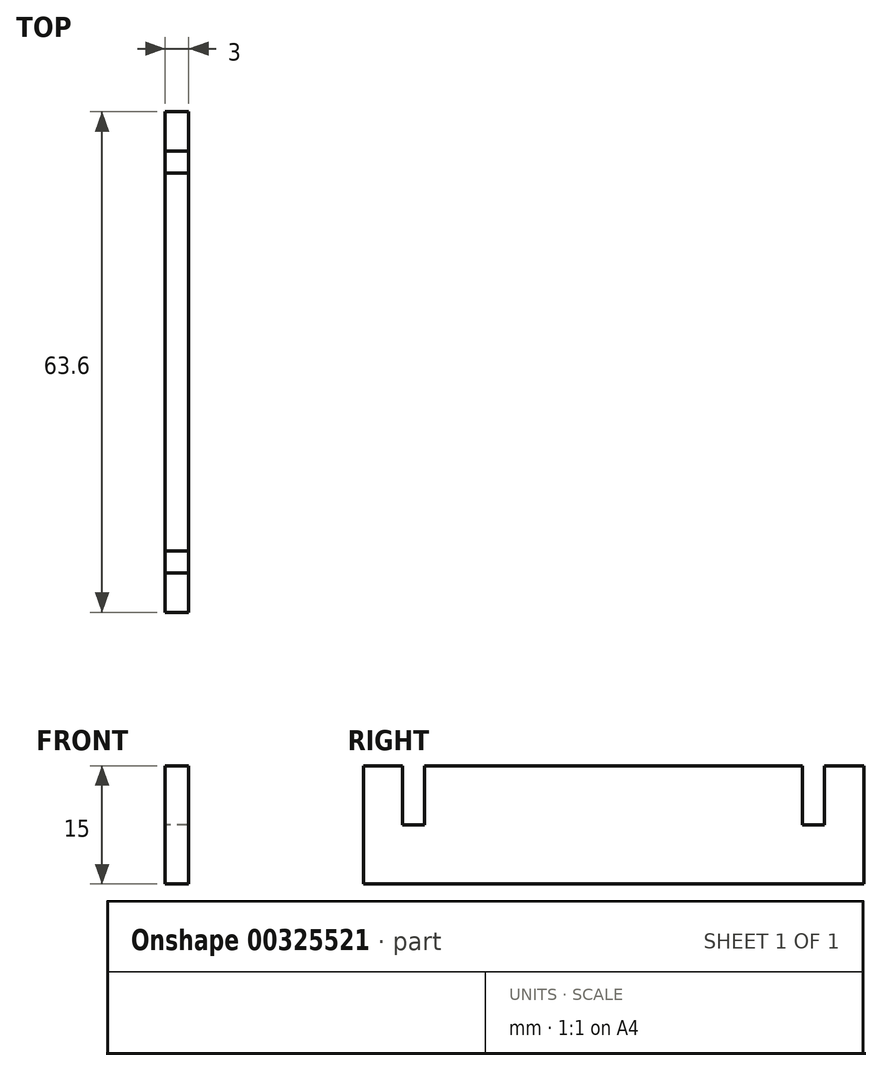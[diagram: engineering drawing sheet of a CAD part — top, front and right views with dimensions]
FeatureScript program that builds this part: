
annotation { "Feature Type Name" : "Feature", "Feature Type Description" : "" }
export const myFeature = defineFeature(function(context is Context, id is Id, definition is map)
    precondition{}
    {
        {
            var Q0;
            Q0=qCreatedBy(makeId("Right.planeOp"),FACE);
            var sketch = newSketch(context, id + "F0", { "sketchPlane" : qUnion([Q0])});
            skLineSegment(sketch, "E0.bottom", {"start": v(31.8, 7.5) * mm, "end": v(26.8, 7.5) * mm});
            skLineSegment(sketch, "E0.top", {"start": v(31.8, -7.5) * mm, "end": v(-31.8, -7.5) * mm});
            skLineSegment(sketch, "E0.left", {"start": v(31.8, 7.5) * mm, "end": v(31.8, -7.5) * mm});
            skLineSegment(sketch, "E0.right", {"start": v(-31.8, 7.5) * mm, "end": v(-31.8, -7.5) * mm});
            skPoint(sketch, "E0.middle", {"position": v(0, 0) * mm});
            skLineSegment(sketch, "E1.top", {"start": v(-26.8, 0) * mm, "end": v(-24, 0) * mm});
            skLineSegment(sketch, "E1.left", {"start": v(-26.8, 7.5) * mm, "end": v(-26.8, 0) * mm});
            skLineSegment(sketch, "E1.right", {"start": v(-24, 7.5) * mm, "end": v(-24, 0) * mm});
            skLineSegment(sketch, "E2.top", {"start": v(26.8, 0) * mm, "end": v(24, 0) * mm});
            skLineSegment(sketch, "E2.left", {"start": v(26.8, 7.5) * mm, "end": v(26.8, 0) * mm});
            skLineSegment(sketch, "E2.right", {"start": v(24, 7.5) * mm, "end": v(24, 0) * mm});
            skLineSegment(sketch, "E3.trimOffspring", {"start": v(24, 7.5) * mm, "end": v(-24, 7.5) * mm});
            skLineSegment(sketch, "E4.trimOffspring", {"start": v(-26.8, 7.5) * mm, "end": v(-31.8, 7.5) * mm});
            skLineSegment(sketch, "E5", {"start": v(0, -7.5) * mm, "end": v(0, 7.5) * mm, "construction": true});
            skSolve(sketch);
        }
        {
            var Q0;
            Q0 = qSketchRegion(id + "F0", true);
            extrude(context, id + "F1", {"entities" : qUnion([Q0]), "depth" : 3 * mm});
        }
    });
